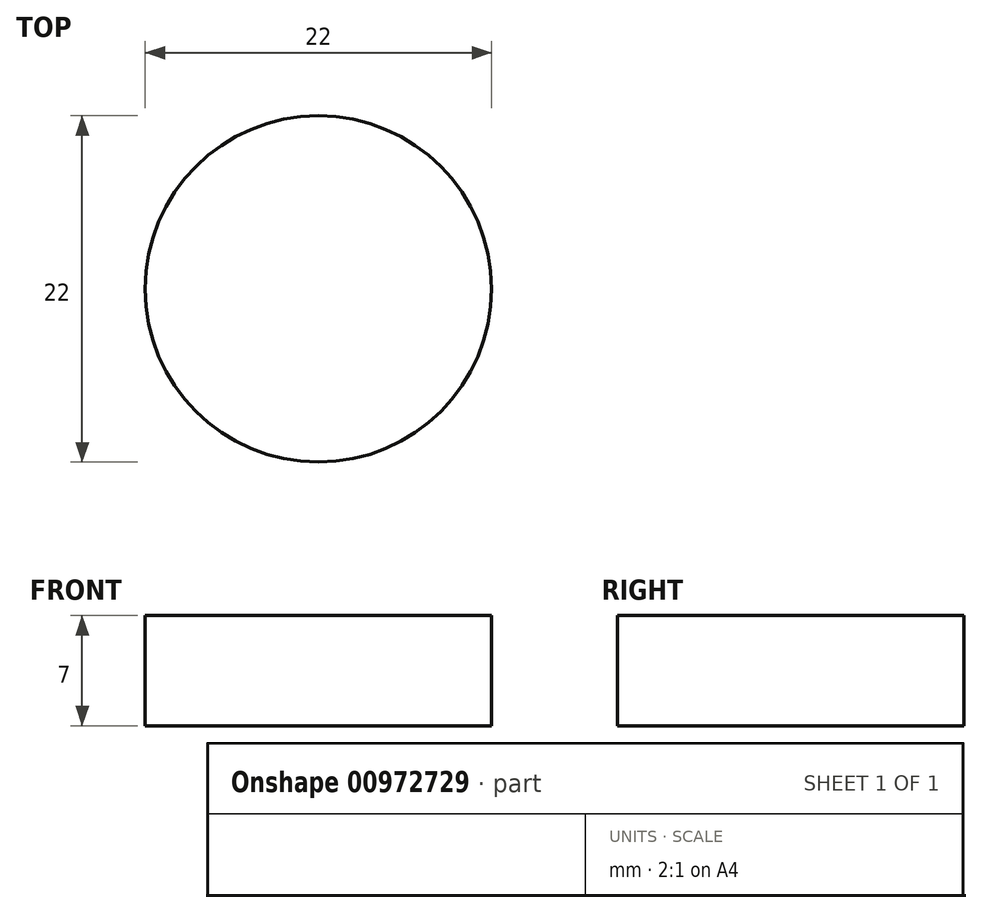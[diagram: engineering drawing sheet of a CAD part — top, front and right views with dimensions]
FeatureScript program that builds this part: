
annotation { "Feature Type Name" : "Feature", "Feature Type Description" : "" }
export const myFeature = defineFeature(function(context is Context, id is Id, definition is map)
    precondition{}
    {
        {
            var Q0;
            Q0=qCreatedBy(makeId("Top.planeOp"),FACE);
            var sketch = newSketch(context, id + "F0", { "sketchPlane" : qUnion([Q0])});
            skCircle(sketch, "E0", {"center": v(-28.53, 17.16) * mm, "radius": 11 * mm});
            skSolve(sketch);
        }
        {
            var Q0;
            Q0=makeQuery(id+"F0.imprint","IMPRINT",FACE,{"disambiguationData":[TD([[makeQuery(id+"F0.imprint","IMPRINT",EDGE,{"derivedFrom":sQuery(id+"F0.wireOp",EDGE,"E0")}),1.0]])]});
            extrude(context, id + "F1", {"entities" : qUnion([Q0]), "depth" : 7 * mm, "offsetDistance" : 25.4 * mm});
        }
    });
